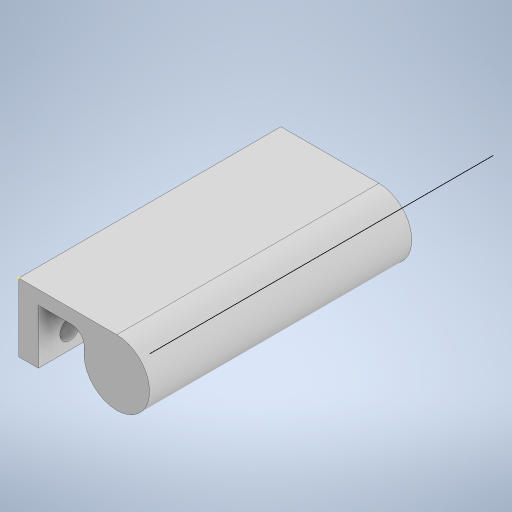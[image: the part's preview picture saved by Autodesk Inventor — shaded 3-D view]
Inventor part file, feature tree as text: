
AUTODESK INVENTOR PART (.ipt)
format: ipt  version: 2024.2 (Build 282272000, 272)  size: 270,848 bytes
history: native  units: in
note: dims shown in document units (in); Inventor stores cm internally (conversion verified against a paired STEP export)
features: sketch x4, extrude x3
ambient origin geometry x8: Origin, YZ Plane, XZ Plane, XY Plane, X Axis, Y Axis, Z Axis, Center Point
bodies: Solid1 (feature_tree)
feature tree (7):
  extrude  "Extrusion1"  Depth=0.65in
  extrude  "Extrusion2"  Depth=0.3937in
  extrude  "Extrusion3"  Depth=0.13in
  sketch  "Sketch4"  dims[d15=0.04in d16=0.0in d17=0.935in d18=0.625in d19=0.125in d20=2.5in d21=0.0in]
  sketch  "Sketch1"  dims[d0=2.5in d1=0.65in]
  sketch  "Sketch2"  dims[d4=2.7559in d6=0.3149in d7=0.3937in d9=1.0in d11=0.3in]
  sketch  "Sketch3"  dims[d12=0.1875in d13=0.0in d14=0.13in]
